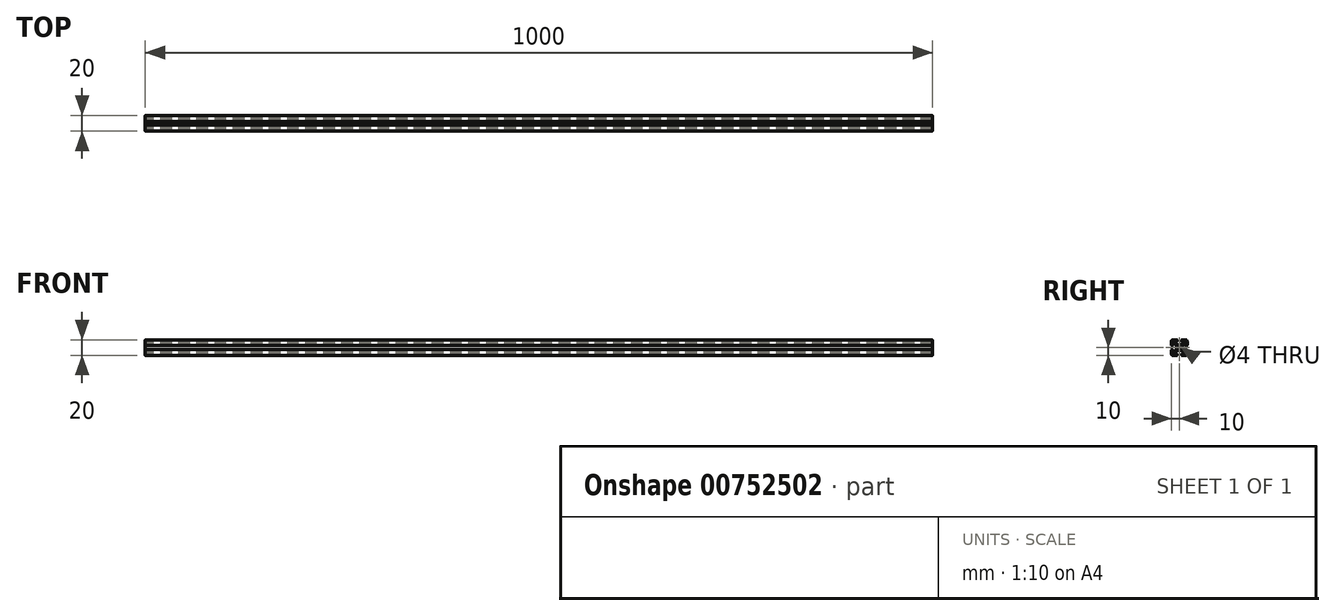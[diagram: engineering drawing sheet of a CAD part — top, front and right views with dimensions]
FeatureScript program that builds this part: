
annotation { "Feature Type Name" : "Feature", "Feature Type Description" : "" }
export const myFeature = defineFeature(function(context is Context, id is Id, definition is map)
    precondition{}
    {
        {
            var Q0;
            Q0=qCreatedBy(makeId("Right.planeOp"),FACE);
            var sketch = newSketch(context, id + "F0", { "sketchPlane" : qUnion([Q0])});
            skLineSegment(sketch, "E0.bottom", {"start": v(-8, 10) * mm, "end": v(-3.3, 10) * mm});
            skLineSegment(sketch, "E0.top", {"start": v(-8, -10) * mm, "end": v(-3.3, -10) * mm});
            skLineSegment(sketch, "E0.right", {"start": v(10, 8) * mm, "end": v(10, 3.3) * mm});
            skLineSegment(sketch, "E1", {"start": v(0, 31.7) * mm, "end": v(0, -24.01) * mm, "construction": true});
            skLineSegment(sketch, "E2", {"start": v(-29.71, 0) * mm, "end": v(21.95, 0) * mm, "construction": true});
            skLineSegment(sketch, "E3", {"start": v(-2.5, 9.2) * mm, "end": v(-2.5, 8.5) * mm});
            skLineSegment(sketch, "E4", {"start": v(-2.8, 8.2) * mm, "end": v(-4.92, 8.2) * mm});
            skLineSegment(sketch, "E5", {"start": v(-5.5, 6.78) * mm, "end": v(-3.25, 4.53) * mm});
            skLineSegment(sketch, "E6", {"start": v(-1.13, 3.65) * mm, "end": v(1.14, 3.65) * mm});
            skLineSegment(sketch, "E7", {"start": v(3.25, 4.53) * mm, "end": v(5.5, 6.78) * mm});
            skLineSegment(sketch, "E8", {"start": v(4.92, 8.2) * mm, "end": v(2.8, 8.2) * mm});
            skLineSegment(sketch, "E9", {"start": v(2.5, 8.5) * mm, "end": v(2.5, 9.2) * mm});
            skLineSegment(sketch, "E10.trimOffspring", {"start": v(3.3, 10) * mm, "end": v(8, 10) * mm});
            skArc(sketch, "E11.filletArc", {"start": v(-8, 10) * mm, "mid": v(-9.41, 9.41) * mm, "end": v(-10, 8) * mm});
            skArc(sketch, "E12.filletArc", {"start": v(-10, -8) * mm, "mid": v(-9.41, -9.41) * mm, "end": v(-8, -10) * mm});
            skArc(sketch, "E13.filletArc", {"start": v(8, -10) * mm, "mid": v(9.41, -9.41) * mm, "end": v(10, -8) * mm});
            skArc(sketch, "E14.filletArc", {"start": v(10, 8) * mm, "mid": v(9.41, 9.41) * mm, "end": v(8, 10) * mm});
            skPoint(sketch, "E15.visualSharp", {"position": v(-9.03, 10.3) * mm});
            skArc(sketch, "E15.filletArc", {"start": v(-4.92, 8.2) * mm, "mid": v(-5.69, 7.69) * mm, "end": v(-5.5, 6.78) * mm});
            skPoint(sketch, "E16.visualSharp", {"position": v(-2.37, 3.65) * mm});
            skArc(sketch, "E16.filletArc", {"start": v(-3.25, 4.53) * mm, "mid": v(-2.28, 3.88) * mm, "end": v(-1.13, 3.65) * mm});
            skPoint(sketch, "E17.visualSharp", {"position": v(2.37, 3.65) * mm});
            skArc(sketch, "E17.filletArc", {"start": v(1.14, 3.65) * mm, "mid": v(2.28, 3.88) * mm, "end": v(3.25, 4.53) * mm});
            skArc(sketch, "E18.filletArc", {"start": v(5.5, 6.78) * mm, "mid": v(5.69, 7.69) * mm, "end": v(4.92, 8.2) * mm});
            skPoint(sketch, "E19.visualSharp", {"position": v(2.5, 8.2) * mm});
            skArc(sketch, "E19.filletArc", {"start": v(2.5, 8.5) * mm, "mid": v(2.59, 8.29) * mm, "end": v(2.8, 8.2) * mm});
            skPoint(sketch, "E20.visualSharp", {"position": v(-2.5, 8.2) * mm});
            skArc(sketch, "E20.filletArc", {"start": v(-2.8, 8.2) * mm, "mid": v(-2.59, 8.29) * mm, "end": v(-2.5, 8.5) * mm});
            skPoint(sketch, "E21.1.5", {"position": v(-3.65, 2.37) * mm});
            skPoint(sketch, "E21.1.13", {"position": v(-10.3, 9.03) * mm});
            skPoint(sketch, "E21.center", {"position": v(0, 0) * mm});
            skLineSegment(sketch, "E22.trimOffspring", {"start": v(-10, -3.3) * mm, "end": v(-10, -8) * mm});
            skLineSegment(sketch, "E23.trimOffspring", {"start": v(10, -3.3) * mm, "end": v(10, -8) * mm});
            skLineSegment(sketch, "E24.trimOffspring", {"start": v(3.3, -10) * mm, "end": v(8, -10) * mm});
            skLineSegment(sketch, "E25", {"start": v(-10, 8) * mm, "end": v(-10, 3.3) * mm});
            skCircle(sketch, "E26", {"center": v(0, 0) * mm, "radius": 2 * mm});
            skPoint(sketch, "E27.visualSharp", {"position": v(-2.5, 10) * mm});
            skArc(sketch, "E27.filletArc", {"start": v(-2.5, 9.2) * mm, "mid": v(-2.73, 9.77) * mm, "end": v(-3.3, 10) * mm});
            skPoint(sketch, "E28.visualSharp", {"position": v(2.5, 10) * mm});
            skArc(sketch, "E28.filletArc", {"start": v(3.3, 10) * mm, "mid": v(2.73, 9.77) * mm, "end": v(2.5, 9.2) * mm});
            skPoint(sketch, "E29.1.1", {"position": v(-10, -2.5) * mm});
            skLineSegment(sketch, "E29.1.2", {"start": v(-3.65, -1.13) * mm, "end": v(-3.65, 1.14) * mm});
            skArc(sketch, "E29.1.3", {"start": v(-4.53, -3.25) * mm, "mid": v(-3.88, -2.28) * mm, "end": v(-3.65, -1.13) * mm});
            skPoint(sketch, "E29.1.4", {"position": v(-8.2, -2.5) * mm});
            skArc(sketch, "E29.1.5", {"start": v(-8.2, -4.92) * mm, "mid": v(-7.69, -5.69) * mm, "end": v(-6.78, -5.5) * mm});
            skLineSegment(sketch, "E29.1.6", {"start": v(-8.2, -2.8) * mm, "end": v(-8.2, -4.92) * mm});
            skLineSegment(sketch, "E29.1.7", {"start": v(-8.2, 4.92) * mm, "end": v(-8.2, 2.8) * mm});
            skArc(sketch, "E29.1.8", {"start": v(-3.65, 1.14) * mm, "mid": v(-3.88, 2.28) * mm, "end": v(-4.53, 3.25) * mm});
            skArc(sketch, "E29.1.9", {"start": v(-6.78, 5.5) * mm, "mid": v(-7.69, 5.69) * mm, "end": v(-8.2, 4.92) * mm});
            skPoint(sketch, "E29.1.10", {"position": v(-3.65, -2.37) * mm});
            skPoint(sketch, "E29.1.11", {"position": v(-10, 2.5) * mm});
            skPoint(sketch, "E29.1.12", {"position": v(-8.2, 2.5) * mm});
            skLineSegment(sketch, "E29.1.13", {"start": v(-6.78, -5.5) * mm, "end": v(-4.53, -3.25) * mm});
            skLineSegment(sketch, "E29.1.14", {"start": v(-4.53, 3.25) * mm, "end": v(-6.78, 5.5) * mm});
            skArc(sketch, "E29.1.15", {"start": v(-10, 3.3) * mm, "mid": v(-9.77, 2.73) * mm, "end": v(-9.2, 2.5) * mm});
            skArc(sketch, "E29.1.16", {"start": v(-9.2, -2.5) * mm, "mid": v(-9.77, -2.73) * mm, "end": v(-10, -3.3) * mm});
            skLineSegment(sketch, "E29.1.17", {"start": v(-8.5, 2.5) * mm, "end": v(-9.2, 2.5) * mm});
            skLineSegment(sketch, "E29.1.18", {"start": v(-9.2, -2.5) * mm, "end": v(-8.5, -2.5) * mm});
            skArc(sketch, "E29.1.19", {"start": v(-8.2, -2.8) * mm, "mid": v(-8.29, -2.59) * mm, "end": v(-8.5, -2.5) * mm});
            skArc(sketch, "E29.1.20", {"start": v(-8.5, 2.5) * mm, "mid": v(-8.29, 2.59) * mm, "end": v(-8.2, 2.8) * mm});
            skPoint(sketch, "E29.2.0", {"position": v(-2.37, -3.65) * mm});
            skPoint(sketch, "E29.2.1", {"position": v(2.5, -10) * mm});
            skLineSegment(sketch, "E29.2.2", {"start": v(1.13, -3.65) * mm, "end": v(-1.14, -3.65) * mm});
            skArc(sketch, "E29.2.3", {"start": v(3.25, -4.53) * mm, "mid": v(2.28, -3.88) * mm, "end": v(1.13, -3.65) * mm});
            skPoint(sketch, "E29.2.4", {"position": v(2.5, -8.2) * mm});
            skArc(sketch, "E29.2.5", {"start": v(4.92, -8.2) * mm, "mid": v(5.69, -7.69) * mm, "end": v(5.5, -6.78) * mm});
            skLineSegment(sketch, "E29.2.6", {"start": v(2.8, -8.2) * mm, "end": v(4.92, -8.2) * mm});
            skLineSegment(sketch, "E29.2.7", {"start": v(-4.92, -8.2) * mm, "end": v(-2.8, -8.2) * mm});
            skArc(sketch, "E29.2.8", {"start": v(-1.14, -3.65) * mm, "mid": v(-2.28, -3.88) * mm, "end": v(-3.25, -4.53) * mm});
            skArc(sketch, "E29.2.9", {"start": v(-5.5, -6.78) * mm, "mid": v(-5.69, -7.69) * mm, "end": v(-4.92, -8.2) * mm});
            skPoint(sketch, "E29.2.10", {"position": v(2.37, -3.65) * mm});
            skPoint(sketch, "E29.2.11", {"position": v(-2.5, -10) * mm});
            skPoint(sketch, "E29.2.12", {"position": v(-2.5, -8.2) * mm});
            skLineSegment(sketch, "E29.2.13", {"start": v(5.5, -6.78) * mm, "end": v(3.25, -4.53) * mm});
            skLineSegment(sketch, "E29.2.14", {"start": v(-3.25, -4.53) * mm, "end": v(-5.5, -6.78) * mm});
            skArc(sketch, "E29.2.15", {"start": v(-3.3, -10) * mm, "mid": v(-2.73, -9.77) * mm, "end": v(-2.5, -9.2) * mm});
            skArc(sketch, "E29.2.16", {"start": v(2.5, -9.2) * mm, "mid": v(2.73, -9.77) * mm, "end": v(3.3, -10) * mm});
            skLineSegment(sketch, "E29.2.17", {"start": v(-2.5, -8.5) * mm, "end": v(-2.5, -9.2) * mm});
            skLineSegment(sketch, "E29.2.18", {"start": v(2.5, -9.2) * mm, "end": v(2.5, -8.5) * mm});
            skArc(sketch, "E29.2.19", {"start": v(2.8, -8.2) * mm, "mid": v(2.59, -8.29) * mm, "end": v(2.5, -8.5) * mm});
            skArc(sketch, "E29.2.20", {"start": v(-2.5, -8.5) * mm, "mid": v(-2.59, -8.29) * mm, "end": v(-2.8, -8.2) * mm});
            skPoint(sketch, "E29.3.0", {"position": v(3.65, -2.37) * mm});
            skPoint(sketch, "E29.3.1", {"position": v(10, 2.5) * mm});
            skLineSegment(sketch, "E29.3.2", {"start": v(3.65, 1.13) * mm, "end": v(3.65, -1.14) * mm});
            skArc(sketch, "E29.3.3", {"start": v(4.53, 3.25) * mm, "mid": v(3.88, 2.28) * mm, "end": v(3.65, 1.13) * mm});
            skPoint(sketch, "E29.3.4", {"position": v(8.2, 2.5) * mm});
            skArc(sketch, "E29.3.5", {"start": v(8.2, 4.92) * mm, "mid": v(7.69, 5.69) * mm, "end": v(6.78, 5.5) * mm});
            skLineSegment(sketch, "E29.3.6", {"start": v(8.2, 2.8) * mm, "end": v(8.2, 4.92) * mm});
            skLineSegment(sketch, "E29.3.7", {"start": v(8.2, -4.92) * mm, "end": v(8.2, -2.8) * mm});
            skArc(sketch, "E29.3.8", {"start": v(3.65, -1.14) * mm, "mid": v(3.88, -2.28) * mm, "end": v(4.53, -3.25) * mm});
            skArc(sketch, "E29.3.9", {"start": v(6.78, -5.5) * mm, "mid": v(7.69, -5.69) * mm, "end": v(8.2, -4.92) * mm});
            skPoint(sketch, "E29.3.10", {"position": v(3.65, 2.37) * mm});
            skPoint(sketch, "E29.3.11", {"position": v(10, -2.5) * mm});
            skPoint(sketch, "E29.3.12", {"position": v(8.2, -2.5) * mm});
            skLineSegment(sketch, "E29.3.13", {"start": v(6.78, 5.5) * mm, "end": v(4.53, 3.25) * mm});
            skLineSegment(sketch, "E29.3.14", {"start": v(4.53, -3.25) * mm, "end": v(6.78, -5.5) * mm});
            skArc(sketch, "E29.3.15", {"start": v(10, -3.3) * mm, "mid": v(9.77, -2.73) * mm, "end": v(9.2, -2.5) * mm});
            skArc(sketch, "E29.3.16", {"start": v(9.2, 2.5) * mm, "mid": v(9.77, 2.73) * mm, "end": v(10, 3.3) * mm});
            skLineSegment(sketch, "E29.3.17", {"start": v(8.5, -2.5) * mm, "end": v(9.2, -2.5) * mm});
            skLineSegment(sketch, "E29.3.18", {"start": v(9.2, 2.5) * mm, "end": v(8.5, 2.5) * mm});
            skArc(sketch, "E29.3.19", {"start": v(8.2, 2.8) * mm, "mid": v(8.29, 2.59) * mm, "end": v(8.5, 2.5) * mm});
            skArc(sketch, "E29.3.20", {"start": v(8.5, -2.5) * mm, "mid": v(8.29, -2.59) * mm, "end": v(8.2, -2.8) * mm});
            skSolve(sketch);
        }
        {
            var Q0;
            Q0=qSketchRegion(id+"F0",true);
            extrude(context, id + "F1", {"entities" : qUnion([Q0]), "depth" : 1000 * mm, "offsetDistance" : 25 * mm});
        }
    });
